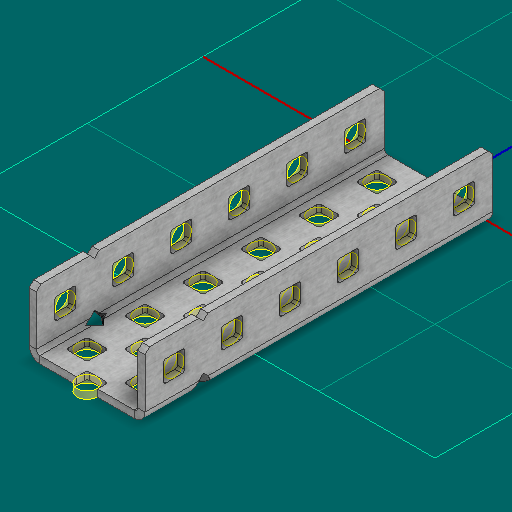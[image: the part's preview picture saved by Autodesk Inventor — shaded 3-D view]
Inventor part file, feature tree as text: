
AUTODESK INVENTOR PART (.ipt)
format: ipt  version: 2025 (Build 290162000, 162)  size: 770,560 bytes
history: native  units: in
note: dims shown in document units (in); Inventor stores cm internally (conversion verified against a paired STEP export)
features: other x66, sketch x5, sheet_metal_op x1
ambient origin geometry x8: Origin, YZ Plane, XZ Plane, XY Plane, X Axis, Y Axis, Z Axis, Center Point
bodies: Solid1 (feature_tree)
feature tree (72):
  other  "Alu C 1x2x1x6.ipt"
  other  "Solid1::Alu C 1x2x1x6.ipt"
  other  "TaggingFeature1"
  sketch  "Sketch1"  dims[d0=0.3937in]
  sketch  "Sketch2"  dims[d1=0.0625in]
  sketch  "Sketch3"
  other  "Flange Pattern Sketch"
  sketch  "Sketch9"
  sheet_metal_op  "Body Pattern Sketch"
  other  "Arc Length"
  sketch  "Sketch14"
  other  "Flange Pattern Plane"
  other  "Srf1"
  other  "Srf2"
  other  "Srf3"
  other  "Srf4"
  other  "Srf5"
  other  "Srf6"
  other  "Srf7"
  other  "Srf8"
  other  "Srf9"
  other  "Srf10"
  other  "Srf11"
  other  "Srf12"
  other  "Srf13"
  other  "Srf14"
  other  "Srf15"
  other  "Srf16"
  other  "Srf17"
  other  "Srf18"
  other  "Srf19"
  other  "Srf20"
  other  "Srf21"
  other  "Srf22"
  other  "Srf23"
  other  "Srf24"
  other  "Srf25"
  other  "Srf26"
  other  "Srf27"
  other  "Srf28"
  other  "Srf29"
  other  "Srf30"
  other  "Srf1::Derived"
  other  "Srf2::Derived"
  other  "Srf823::Derived"
  other  "Srf824::Derived"
  other  "Srf825::Derived"
  other  "Srf826::Derived"
  other  "Srf827::Derived"
  other  "Srf828::Derived"
  other  "Srf829::Derived"
  other  "Srf922::Derived"
  other  "Srf923::Derived"
  other  "Srf924::Derived"
  other  "Srf91::Derived"
  other  "Srf92::Derived"
  other  "Srf856::Derived"
  other  "Srf857::Derived"
  other  "Srf858::Derived"
  other  "Srf859::Derived"
  other  "Srf860::Derived"
  other  "Srf861::Derived"
  other  "Srf862::Derived"
  other  "Srf959::Derived"
  other  "Srf960::Derived"
  other  "Srf961::Derived"
  other  "Srf786::Derived"
  other  "Srf889::Derived"
  other  "Srf890::Derived"
  other  "Srf891::Derived"
  other  "Srf892::Derived"
  other  "Srf893::Derived"
